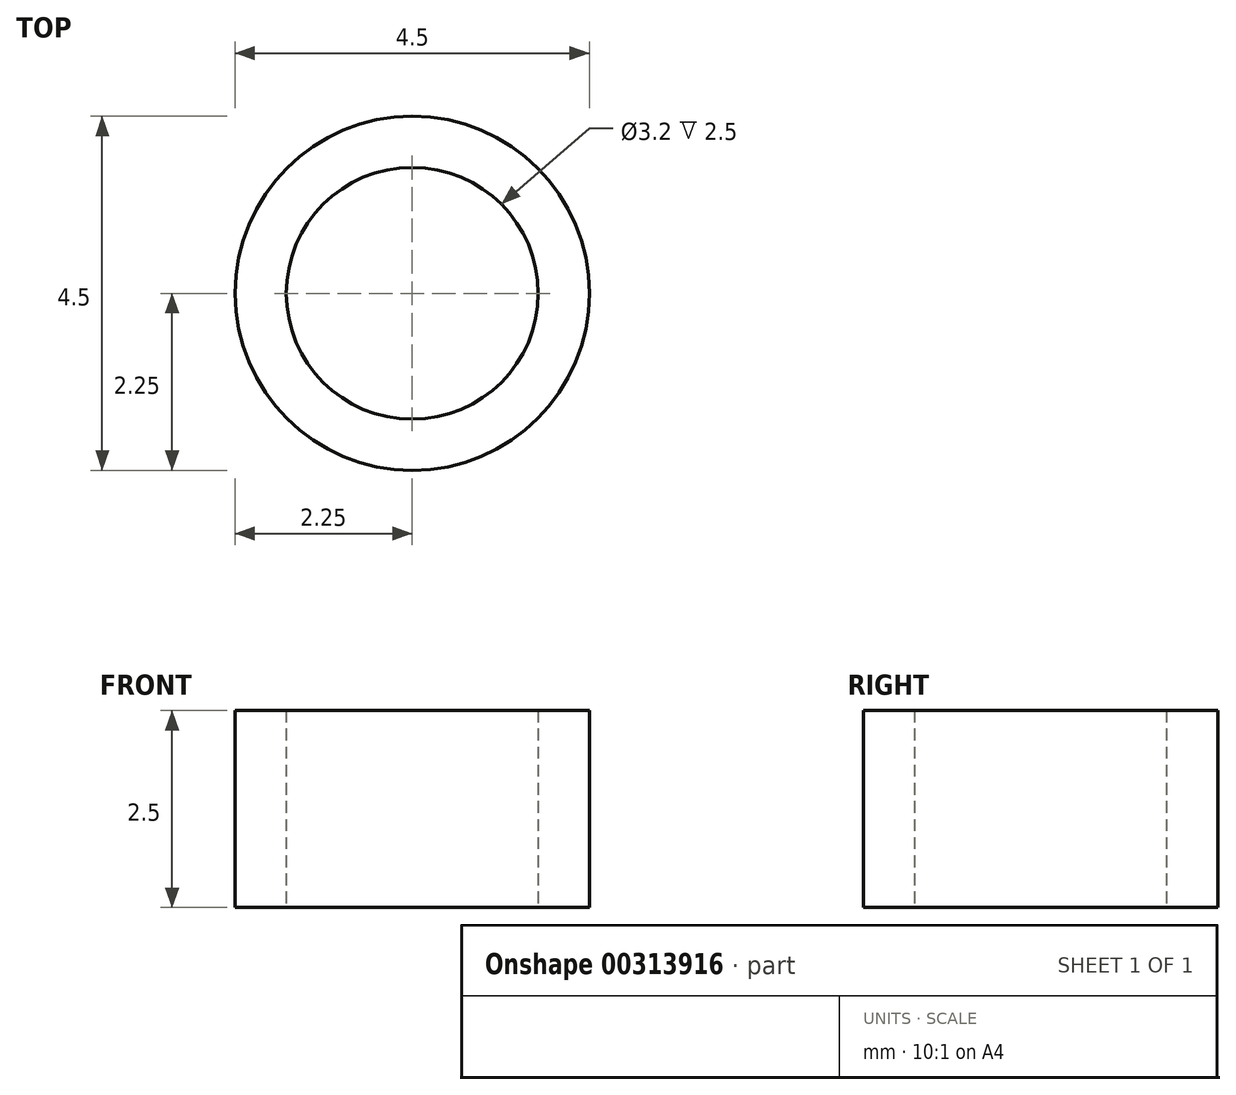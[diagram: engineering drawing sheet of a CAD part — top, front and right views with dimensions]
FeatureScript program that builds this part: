
annotation { "Feature Type Name" : "Feature", "Feature Type Description" : "" }
export const myFeature = defineFeature(function(context is Context, id is Id, definition is map)
    precondition{}
    {
        {
            var Q0;
            Q0=qCreatedBy(makeId("Top.planeOp"),FACE);
            var sketch = newSketch(context, id + "F0", { "sketchPlane" : qUnion([Q0])});
            skCircle(sketch, "E0", {"center": v(0, 0) * mm, "radius": 2.25 * mm});
            skCircle(sketch, "E1", {"center": v(0, 0) * mm, "radius": 1.6 * mm});
            skSolve(sketch);
        }
        {
            var Q0;
            Q0 = qSketchRegion(id + "F0", true);
            extrude(context, id + "F1", {"entities" : qUnion([Q0]), "depth" : 2.5 * mm, "offsetDistance" : 25 * mm});
        }
    });
